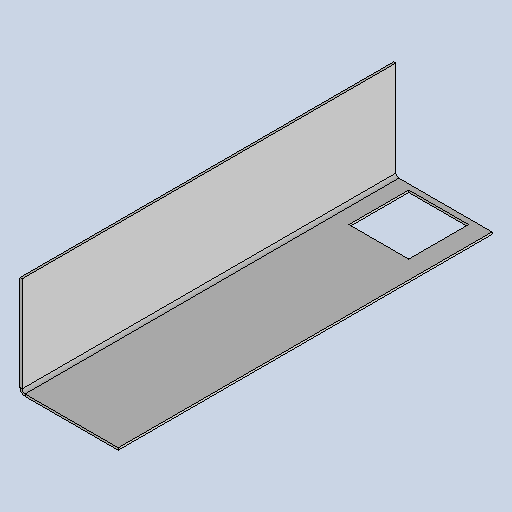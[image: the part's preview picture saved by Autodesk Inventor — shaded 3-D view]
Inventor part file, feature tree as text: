
AUTODESK INVENTOR PART (.ipt)
format: ipt  version: 2025.1 (Build 291241020, 241B)  size: 170,496 bytes
history: native  units: mm
features: sheet_metal_op x4, other x4, sketch x3
ambient origin geometry x8: Origin, YZ Plane, XZ Plane, XY Plane, X Axis, Y Axis, Z Axis, Center Point
bodies: Body1 (feature_tree)
feature tree (11):
  sheet_metal_op  "Face3"
  sheet_metal_op  "Flange3"
  sketch  "Sketch1"  dims[d154=92.0mm]
  other  "Plate5"
  sketch  "Sketch7"  dims[d155=350.0mm]
  other  "Plate6"
  sheet_metal_op  "Bend3"
  sheet_metal_op  "Corner3"
  sketch  "Sketch8"  dims[d156=2.0mm d157=2.0mm d158=1.0mm d159=4.0mm d160=2.75mm d161=94.0mm d162=90.0deg d163=2.75mm d164=8.0mm d165=2.0mm d166=2.75mm d167=56.0mm d168=56.0mm d169=5.0mm d170=2.0mm d171=0.0mm d172=17.0mm]
  other  "Cut1"
  other  "Definition1"
